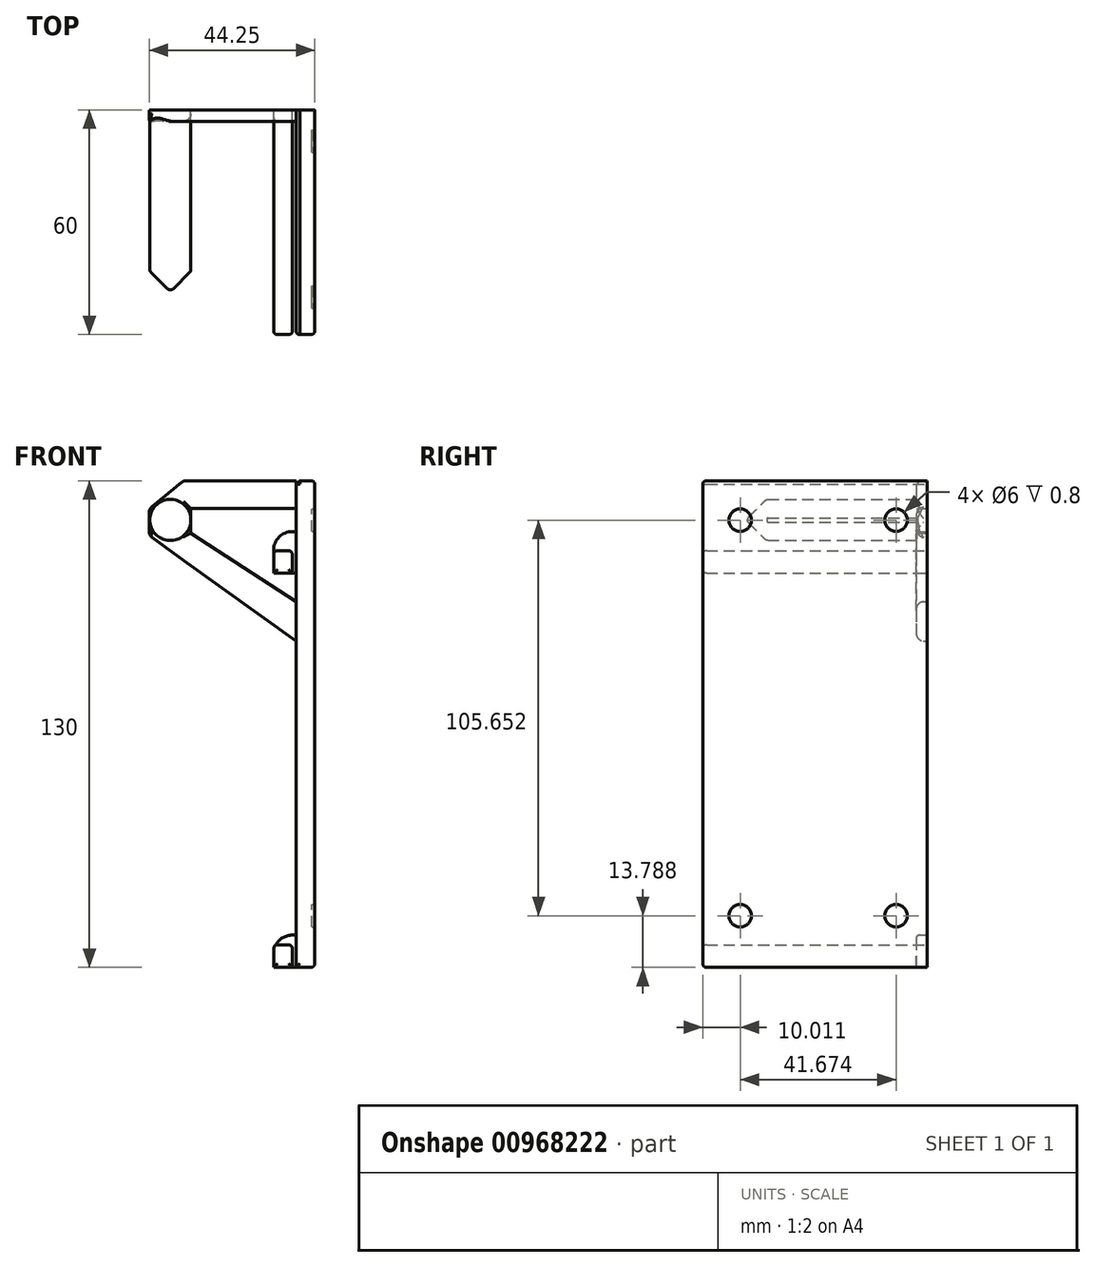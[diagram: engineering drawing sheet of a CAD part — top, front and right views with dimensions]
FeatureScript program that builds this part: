
annotation { "Feature Type Name" : "Feature", "Feature Type Description" : "" }
export const myFeature = defineFeature(function(context is Context, id is Id, definition is map)
    precondition{}
    {
        {
            var Q0;
            Q0=qCreatedBy(makeId("Front.planeOp"),FACE);
            var sketch = newSketch(context, id + "F0", { "sketchPlane" : qUnion([Q0])});
            skLineSegment(sketch, "E0.bottom", {"start": v(0, 55.56) * mm, "end": v(-5, 55.56) * mm});
            skLineSegment(sketch, "E0.top", {"start": v(0, -74.44) * mm, "end": v(-5, -74.44) * mm});
            skLineSegment(sketch, "E0.left", {"start": v(0, 55.56) * mm, "end": v(0, -74.44) * mm});
            skLineSegment(sketch, "E0.right", {"start": v(-5, 55.56) * mm, "end": v(-5, -74.44) * mm});
            skLineSegment(sketch, "E1", {"start": v(-5, 55.56) * mm, "end": v(-35, 55.56) * mm});
            skLineSegment(sketch, "E2", {"start": v(-35, 55.56) * mm, "end": v(-44.25, 47.98) * mm});
            skLineSegment(sketch, "E3", {"start": v(-44.25, 47.98) * mm, "end": v(-44.25, 40.95) * mm});
            skLineSegment(sketch, "E4", {"start": v(-44.25, 40.95) * mm, "end": v(-35, 34.13) * mm});
            skLineSegment(sketch, "E5", {"start": v(-35, 34.13) * mm, "end": v(-5, 12.72) * mm});
            skLineSegment(sketch, "E6", {"start": v(-5, 12.72) * mm, "end": v(-5, 23.2) * mm});
            skLineSegment(sketch, "E7", {"start": v(-5, 23.2) * mm, "end": v(-33.14, 41.58) * mm});
            skLineSegment(sketch, "E8", {"start": v(-33.14, 41.58) * mm, "end": v(-33.14, 48.1) * mm});
            skLineSegment(sketch, "E9", {"start": v(-33.14, 48.1) * mm, "end": v(-5, 48.1) * mm});
            skLineSegment(sketch, "E10", {"start": v(-5, 48.1) * mm, "end": v(-5, 55.56) * mm});
            skLineSegment(sketch, "E11", {"start": v(-5, 23.2) * mm, "end": v(-5, 12.72) * mm});
            skLineSegment(sketch, "E12", {"start": v(-5, -74.44) * mm, "end": v(-6, -74.44) * mm});
            skLineSegment(sketch, "E13", {"start": v(-6, -74.44) * mm, "end": v(-11, -74.44) * mm});
            skLineSegment(sketch, "E14", {"start": v(-11, -74.44) * mm, "end": v(-11, -68.44) * mm});
            skLineSegment(sketch, "E15", {"start": v(-11, -68.44) * mm, "end": v(-6, -68.44) * mm});
            skLineSegment(sketch, "E16", {"start": v(-6, -68.44) * mm, "end": v(-6, -74.44) * mm});
            skLineSegment(sketch, "E17.bottom", {"start": v(-5, -74.44) * mm, "end": v(-11, -74.44) * mm});
            skLineSegment(sketch, "E17.top", {"start": v(-5, -65.81) * mm, "end": v(-11, -65.81) * mm});
            skLineSegment(sketch, "E17.left", {"start": v(-5, -74.44) * mm, "end": v(-5, -65.81) * mm});
            skLineSegment(sketch, "E17.right", {"start": v(-11, -74.44) * mm, "end": v(-11, -65.81) * mm});
            skLineSegment(sketch, "E18", {"start": v(-5, 30.82) * mm, "end": v(-6, 30.82) * mm});
            skLineSegment(sketch, "E19", {"start": v(-6, 30.82) * mm, "end": v(-11, 30.82) * mm});
            skLineSegment(sketch, "E20", {"start": v(-11, 30.82) * mm, "end": v(-11, 36.82) * mm});
            skLineSegment(sketch, "E21", {"start": v(-11, 36.82) * mm, "end": v(-6, 36.82) * mm});
            skLineSegment(sketch, "E22", {"start": v(-6, 36.82) * mm, "end": v(-6, 30.82) * mm});
            skLineSegment(sketch, "E23.bottom", {"start": v(-5, 30.82) * mm, "end": v(-11, 30.82) * mm});
            skLineSegment(sketch, "E23.top", {"start": v(-5, 41.97) * mm, "end": v(-11, 41.97) * mm});
            skLineSegment(sketch, "E23.left", {"start": v(-5, 30.82) * mm, "end": v(-5, 41.97) * mm});
            skLineSegment(sketch, "E23.right", {"start": v(-11, 30.82) * mm, "end": v(-11, 41.97) * mm});
            skSolve(sketch);
        }
        {
            var Q0;
            {var subQ4=sQuery(id+"F0.wireOp",EDGE,"E21");Q0=makeQuery(id+"F0.imprint","IMPRINT",FACE,{"disambiguationData":[TD([[makeQuery(id+"F0.imprint","IMPRINT",EDGE,{"derivedFrom":subQ4}),1.0]])]});}
            var Q1;
            Q1=makeQuery(id+"F0.imprint","IMPRINT",FACE,{"disambiguationData":[TD([[makeQuery(id+"F0.imprint","IMPRINT",EDGE,{"derivedFrom":sQuery(id+"F0.wireOp",EDGE,"E1")}),1.0]])]});
            var Q2;
            {var subQ4=sQuery(id+"F0.wireOp",EDGE,"E15");Q2=makeQuery(id+"F0.imprint","IMPRINT",FACE,{"disambiguationData":[TD([[makeQuery(id+"F0.imprint","IMPRINT",EDGE,{"derivedFrom":subQ4}),1.0]])]});}
            var Q3;
            {var subQ0=sQuery(id+"F0.wireOp",EDGE,"E15");Q3=makeQuery(id+"F0.imprint","IMPRINT",FACE,{"disambiguationData":[TD([[makeQuery(id+"F0.imprint","IMPRINT",EDGE,{"derivedFrom":subQ0}),-1.0]])]});}
            var Q4;
            {var subQ0=sQuery(id+"F0.wireOp",EDGE,"E21");Q4=makeQuery(id+"F0.imprint","IMPRINT",FACE,{"disambiguationData":[TD([[makeQuery(id+"F0.imprint","IMPRINT",EDGE,{"derivedFrom":subQ0}),-1.0]])]});}
            extrude(context, id + "F1", {"entities" : qUnion([Q0, Q1, Q2, Q3, Q4]), "depth" : 3 * mm, "offsetDistance" : 25 * mm});
        }
        {
            var Q0;
            Q0=makeQuery(id+"F0.imprint","IMPRINT",FACE,{"disambiguationData":[TD([[makeQuery(id+"F0.imprint","IMPRINT",EDGE,{"derivedFrom":sQuery(id+"F0.wireOp",EDGE,"E0.bottom")}),1.0]])]});
            var Q1;
            {var subQ0=sQuery(id+"F0.wireOp",EDGE,"E15");Q1=makeQuery(id+"F0.imprint","IMPRINT",FACE,{"disambiguationData":[TD([[makeQuery(id+"F0.imprint","IMPRINT",EDGE,{"derivedFrom":subQ0}),-1.0]])]});}
            var Q2;
            {var subQ0=sQuery(id+"F0.wireOp",EDGE,"E21");Q2=makeQuery(id+"F0.imprint","IMPRINT",FACE,{"disambiguationData":[TD([[makeQuery(id+"F0.imprint","IMPRINT",EDGE,{"derivedFrom":subQ0}),-1.0]])]});}
            extrude(context, id + "F2", {"entities" : qUnion([Q0, Q1, Q2]), "depth" : 60 * mm, "offsetDistance" : 25 * mm});
        }
        {
            var Q0;
            Q0=makeQuery(id+"F1.opExtrude","CAP_FACE",FACE,{"disambiguationData":[OSD([sQuery(id+"F0.wireOp",EDGE,"E1"),sQuery(id+"F0.wireOp",EDGE,"E2"),sQuery(id+"F0.wireOp",EDGE,"E3"),sQuery(id+"F0.wireOp",EDGE,"E4"),sQuery(id+"F0.wireOp",EDGE,"E5"),sQuery(id+"F0.wireOp",EDGE,"E7"),sQuery(id+"F0.wireOp",EDGE,"E8"),sQuery(id+"F0.wireOp",EDGE,"E9"),sQuery(id+"F0.wireOp",EDGE,"E10"),sQuery(id+"F0.wireOp",EDGE,"E11")])],"isStart":false});
            var sketch = newSketch(context, id + "F3", { "sketchPlane" : qUnion([Q0])});
            skCircle(sketch, "E24", {"center": v(-38.6, 45.06) * mm, "radius": 5.5 * mm});
            skSolve(sketch);
        }
        {
            var Q0;
            {var subQ0=sQuery(id+"F3.wireOp",EDGE,"E24");var subQ1=makeQuery(id+"F1.opExtrude","CAP_EDGE",EDGE,{"disambiguationData":[OSD([sQuery(id+"F0.wireOp",EDGE,"E8")])],"isStart":false});var subQ2=makeQuery(id+"F3.imprint","INTERSECT",VERTEX,{"disambiguationData":[OD(0.0)],"derivedFrom":[subQ1,subQ0]});Q0=makeQuery(id+"F3.imprint","IMPRINT",FACE,{"disambiguationData":[TD([[makeQuery(id+"F3.imprint","IMPRINT",EDGE,{"disambiguationData":[TD([[subQ2,1.0]])],"derivedFrom":subQ0}),1.0]])]});}
            extrude(context, id + "F4", {"entities" : qUnion([Q0]), "operationType" : NewBodyOperationType.ADD, "depth" : 45 * mm, "offsetDistance" : 25 * mm});
        }
        {
            var Q0;
            Q0=makeQuery(id+"F4.opExtrude","CAP_EDGE",EDGE,{"disambiguationData":[OSD([sQuery(id+"F3.wireOp",EDGE,"E24")])],"isStart":false});
            chamfer(context, id + "F5", {"entities" : qUnion([Q0]), "width" : 5 * mm, "tangentPropagation" : true});
        }
        {
            var Q0;
            Q0=makeQuery(id+"F1.opExtrude","SWEPT_EDGE",EDGE,{"disambiguationData":[OSD([sQuery(id+"F0.wireOp",EDGE,"E2"),sQuery(id+"F0.wireOp",EDGE,"E3")])]});
            var Q1;
            Q1=makeQuery(id+"F1.opExtrude","SWEPT_EDGE",EDGE,{"disambiguationData":[OSD([sQuery(id+"F0.wireOp",EDGE,"E3"),sQuery(id+"F0.wireOp",EDGE,"E4")])]});
            var Q2;
            Q2=makeQuery(id+"F1.opExtrude","SWEPT_EDGE",EDGE,{"disambiguationData":[OSD([sQuery(id+"F0.wireOp",EDGE,"E1"),sQuery(id+"F0.wireOp",EDGE,"E2")])]});
            var Q3;
            Q3=makeQuery(id+"F1.opExtrude","SWEPT_EDGE",EDGE,{"disambiguationData":[OSD([sQuery(id+"F0.wireOp",EDGE,"E4"),sQuery(id+"F0.wireOp",EDGE,"E5")])]});
            var Q4;
            Q4=makeQuery(id+"F1.opExtrude","CAP_EDGE",EDGE,{"disambiguationData":[OSD([sQuery(id+"F0.wireOp",EDGE,"E5")])],"isStart":false});
            var Q5;
            Q5=makeQuery(id+"F1.opExtrude","CAP_EDGE",EDGE,{"disambiguationData":[OSD([sQuery(id+"F0.wireOp",EDGE,"E7")])],"isStart":false});
            var Q6;
            Q6=makeQuery(id+"F1.opExtrude","CAP_EDGE",EDGE,{"disambiguationData":[OSD([sQuery(id+"F0.wireOp",EDGE,"E4")])],"isStart":false});
            var Q7;
            Q7=makeQuery(id+"F1.opExtrude","CAP_EDGE",EDGE,{"disambiguationData":[OSD([sQuery(id+"F0.wireOp",EDGE,"E1")])],"isStart":false});
            var Q8;
            Q8=makeQuery(id+"F1.opExtrude","CAP_EDGE",EDGE,{"disambiguationData":[OSD([sQuery(id+"F0.wireOp",EDGE,"E9")])],"isStart":false});
            var Q9;
            {var subQ0=sQuery(id+"F0.wireOp",EDGE,"E8");var subQ1=sQuery(id+"F0.wireOp",EDGE,"E7");Q9=makeQuery(id+"F4.boolean.opBoolean","SPLIT",EDGE,{"disambiguationData":[TD([makeQuery(id+"F1.opExtrude","SWEPT_FACE",FACE,{"disambiguationData":[OSD([subQ1])]})])],"derivedFrom":makeQuery(id+"F1.opExtrude","CAP_EDGE",EDGE,{"disambiguationData":[OSD([subQ0])],"isStart":false})});}
            var Q10;
            {var subQ0=sQuery(id+"F0.wireOp",EDGE,"E9");var subQ1=sQuery(id+"F0.wireOp",EDGE,"E8");Q10=makeQuery(id+"F4.boolean.opBoolean","SPLIT",EDGE,{"disambiguationData":[TD([makeQuery(id+"F1.opExtrude","SWEPT_FACE",FACE,{"disambiguationData":[OSD([subQ0])]})])],"derivedFrom":makeQuery(id+"F1.opExtrude","CAP_EDGE",EDGE,{"disambiguationData":[OSD([subQ1])],"isStart":false})});}
            var Q11;
            Q11=makeQuery(id+"F1.opExtrude","CAP_EDGE",EDGE,{"disambiguationData":[OSD([sQuery(id+"F0.wireOp",EDGE,"E2")])],"isStart":false});
            fillet(context, id + "F6", {"entities" : qUnion([Q0, Q1, Q2, Q3, Q4, Q5, Q6, Q7, Q8, Q9, Q10, Q11]), "radius" : 2 * mm, "tangentPropagation" : true, "allowEdgeOverflow" : false});
        }
        {
            var Q0;
            Q0=makeQuery(id+"F1.opExtrude","CAP_EDGE",EDGE,{"disambiguationData":[OSD([sQuery(id+"F0.wireOp",EDGE,"E3")])],"isStart":false});
            var Q1;
            {var subQ0=sQuery(id+"F3.wireOp",EDGE,"E24");Q1=makeQuery(id+"F5.opChamfer","BLEND_EDGE",EDGE,{"blendedFrom":[makeQuery(id+"F4.opExtrude","CAP_EDGE",EDGE,{"disambiguationData":[OSD([subQ0])],"isStart":false}),makeQuery(id+"F4.opExtrude","SWEPT_FACE",FACE,{"disambiguationData":[OSD([subQ0])]})],"blendedInto":[makeQuery(id+"F4.opExtrude","SWEPT_FACE",FACE,{"disambiguationData":[OSD([subQ0])]})]});}
            var Q2;
            {var subQ0=sQuery(id+"F3.wireOp",EDGE,"E24");Q2=makeQuery(id+"F5.opChamfer","BLEND_EDGE",EDGE,{"blendedFrom":[makeQuery(id+"F4.opExtrude","CAP_EDGE",EDGE,{"disambiguationData":[OSD([subQ0])],"isStart":false}),makeQuery(id+"F4.opExtrude","CAP_FACE",FACE,{"disambiguationData":[OSD([sQuery(id+"F0.wireOp",EDGE,"E8"),subQ0])],"isStart":false})],"blendedInto":[makeQuery(id+"F4.opExtrude","CAP_FACE",FACE,{"disambiguationData":[OSD([sQuery(id+"F0.wireOp",EDGE,"E8"),subQ0])],"isStart":false})]});}
            var Q3;
            Q3=makeQuery(id+"F2.opExtrude","SWEPT_EDGE",EDGE,{"disambiguationData":[OSD([sQuery(id+"F0.wireOp",EDGE,"E21"),sQuery(id+"F0.wireOp",EDGE,"E22")])]});
            var Q4;
            Q4=makeQuery(id+"F2.opExtrude","SWEPT_EDGE",EDGE,{"disambiguationData":[OSD([sQuery(id+"F0.wireOp",EDGE,"E21"),sQuery(id+"F0.wireOp",EDGE,"E23.right")])]});
            var Q5;
            Q5=makeQuery(id+"F2.opExtrude","SWEPT_EDGE",EDGE,{"disambiguationData":[OSD([sQuery(id+"F0.wireOp",EDGE,"E23.bottom"),sQuery(id+"F0.wireOp",EDGE,"E23.right")])]});
            var Q6;
            Q6=makeQuery(id+"F2.opExtrude","SWEPT_EDGE",EDGE,{"disambiguationData":[OSD([sQuery(id+"F0.wireOp",EDGE,"E22"),sQuery(id+"F0.wireOp",EDGE,"E23.bottom")])]});
            var Q7;
            Q7=makeQuery(id+"F1.opExtrude","CAP_EDGE",EDGE,{"disambiguationData":[OSD([sQuery(id+"F0.wireOp",EDGE,"E23.right")])],"isStart":false});
            var Q8;
            Q8=makeQuery(id+"F1.opExtrude","CAP_EDGE",EDGE,{"disambiguationData":[OSD([sQuery(id+"F0.wireOp",EDGE,"E23.top")])],"isStart":false});
            var Q9;
            Q9=makeQuery(id+"F1.opExtrude","CAP_EDGE",EDGE,{"disambiguationData":[OSD([sQuery(id+"F0.wireOp",EDGE,"E23.bottom")])],"isStart":false});
            var Q10;
            Q10=makeQuery(id+"F2.opExtrude","SWEPT_EDGE",EDGE,{"disambiguationData":[OSD([sQuery(id+"F0.wireOp",EDGE,"E15"),sQuery(id+"F0.wireOp",EDGE,"E17.right")])]});
            var Q11;
            Q11=makeQuery(id+"F2.opExtrude","SWEPT_EDGE",EDGE,{"disambiguationData":[OSD([sQuery(id+"F0.wireOp",EDGE,"E17.bottom"),sQuery(id+"F0.wireOp",EDGE,"E17.right")])]});
            var Q12;
            Q12=makeQuery(id+"F2.opExtrude","SWEPT_EDGE",EDGE,{"disambiguationData":[OSD([sQuery(id+"F0.wireOp",EDGE,"E15"),sQuery(id+"F0.wireOp",EDGE,"E16")])]});
            var Q13;
            Q13=makeQuery(id+"F2.opExtrude","SWEPT_EDGE",EDGE,{"disambiguationData":[OSD([sQuery(id+"F0.wireOp",EDGE,"E16"),sQuery(id+"F0.wireOp",EDGE,"E17.bottom")])]});
            var Q14;
            Q14=makeQuery(id+"F2.opExtrude","CAP_FACE",FACE,{"disambiguationData":[OSD([sQuery(id+"F0.wireOp",EDGE,"E15"),sQuery(id+"F0.wireOp",EDGE,"E16"),sQuery(id+"F0.wireOp",EDGE,"E17.bottom"),sQuery(id+"F0.wireOp",EDGE,"E17.right")])],"isStart":false});
            var Q15;
            Q15=makeQuery(id+"F2.opExtrude","CAP_FACE",FACE,{"disambiguationData":[OSD([sQuery(id+"F0.wireOp",EDGE,"E21"),sQuery(id+"F0.wireOp",EDGE,"E22"),sQuery(id+"F0.wireOp",EDGE,"E23.bottom"),sQuery(id+"F0.wireOp",EDGE,"E23.right")])],"isStart":false});
            var Q16;
            Q16=makeQuery(id+"F2.opExtrude","CAP_EDGE",EDGE,{"disambiguationData":[OSD([sQuery(id+"F0.wireOp",EDGE,"E0.right"),sQuery(id+"F0.wireOp",EDGE,"E10"),sQuery(id+"F0.wireOp",EDGE,"E11"),sQuery(id+"F0.wireOp",EDGE,"E17.left"),sQuery(id+"F0.wireOp",EDGE,"E23.left")])],"isStart":false});
            var Q17;
            Q17=makeQuery(id+"F2.opExtrude","CAP_EDGE",EDGE,{"disambiguationData":[OSD([sQuery(id+"F0.wireOp",EDGE,"E0.left")])],"isStart":false});
            var Q18;
            Q18=makeQuery(id+"F2.opExtrude","CAP_EDGE",EDGE,{"disambiguationData":[OSD([sQuery(id+"F0.wireOp",EDGE,"E0.top")])],"isStart":false});
            var Q19;
            Q19=makeQuery(id+"F2.opExtrude","CAP_EDGE",EDGE,{"disambiguationData":[OSD([sQuery(id+"F0.wireOp",EDGE,"E0.bottom")])],"isStart":false});
            var Q20;
            Q20=makeQuery(id+"F2.opExtrude","SWEPT_EDGE",EDGE,{"disambiguationData":[OSD([sQuery(id+"F0.wireOp",EDGE,"E0.bottom"),sQuery(id+"F0.wireOp",EDGE,"E0.left")])]});
            var Q21;
            Q21=makeQuery(id+"F2.opExtrude","SWEPT_EDGE",EDGE,{"disambiguationData":[OSD([sQuery(id+"F0.wireOp",EDGE,"E0.top"),sQuery(id+"F0.wireOp",EDGE,"E0.left")])]});
            var Q22;
            Q22=makeQuery(id+"F1.opExtrude","CAP_EDGE",EDGE,{"disambiguationData":[OSD([sQuery(id+"F0.wireOp",EDGE,"E17.right")])],"isStart":false});
            var Q23;
            Q23=makeQuery(id+"F1.opExtrude","CAP_EDGE",EDGE,{"disambiguationData":[OSD([sQuery(id+"F0.wireOp",EDGE,"E17.top")])],"isStart":false});
            var Q24;
            Q24=makeQuery(id+"F1.opExtrude","CAP_EDGE",EDGE,{"disambiguationData":[OSD([sQuery(id+"F0.wireOp",EDGE,"E17.bottom")])],"isStart":false});
            fillet(context, id + "F7", {"entities" : qUnion([Q0, Q1, Q2, Q3, Q4, Q5, Q6, Q7, Q8, Q9, Q10, Q11, Q12, Q13, Q14, Q15, Q16, Q17, Q18, Q19, Q20, Q21, Q22, Q23, Q24]), "radius" : 1 * mm, "tangentPropagation" : true, "allowEdgeOverflow" : false});
        }
        {
            var Q0;
            Q0=makeQuery(id+"F2.opExtrude","SWEPT_FACE",FACE,{"disambiguationData":[OSD([sQuery(id+"F0.wireOp",EDGE,"E0.left")])]});
            var sketch = newSketch(context, id + "F8", { "sketchPlane" : qUnion([Q0])});
            skLineSegment(sketch, "E25.bottom", {"start": v(-8.32, -60.65) * mm, "end": v(-49.99, -60.65) * mm, "construction": true});
            skLineSegment(sketch, "E25.top", {"start": v(-8.32, 45) * mm, "end": v(-49.99, 45) * mm, "construction": true});
            skLineSegment(sketch, "E25.left", {"start": v(-8.32, -60.65) * mm, "end": v(-8.32, 45) * mm, "construction": true});
            skLineSegment(sketch, "E25.right", {"start": v(-49.99, -60.65) * mm, "end": v(-49.99, 45) * mm, "construction": true});
            skCircle(sketch, "E26", {"center": v(-49.99, 45) * mm, "radius": 3 * mm});
            skCircle(sketch, "E27", {"center": v(-8.32, 45) * mm, "radius": 3 * mm});
            skCircle(sketch, "E28", {"center": v(-49.99, -60.65) * mm, "radius": 3 * mm});
            skCircle(sketch, "E29", {"center": v(-8.32, -60.65) * mm, "radius": 3 * mm});
            skSolve(sketch);
        }
        {
            var Q0;
            Q0=makeQuery(id+"F8.imprint","IMPRINT",FACE,{"disambiguationData":[TD([[makeQuery(id+"F8.imprint","IMPRINT",EDGE,{"derivedFrom":sQuery(id+"F8.wireOp",EDGE,"E26")}),1.0]])]});
            var Q1;
            Q1=makeQuery(id+"F8.imprint","IMPRINT",FACE,{"disambiguationData":[TD([[makeQuery(id+"F8.imprint","IMPRINT",EDGE,{"derivedFrom":sQuery(id+"F8.wireOp",EDGE,"E27")}),1.0]])]});
            var Q2;
            Q2=makeQuery(id+"F8.imprint","IMPRINT",FACE,{"disambiguationData":[TD([[makeQuery(id+"F8.imprint","IMPRINT",EDGE,{"derivedFrom":sQuery(id+"F8.wireOp",EDGE,"E28")}),1.0]])]});
            var Q3;
            Q3=makeQuery(id+"F8.imprint","IMPRINT",FACE,{"disambiguationData":[TD([[makeQuery(id+"F8.imprint","IMPRINT",EDGE,{"derivedFrom":sQuery(id+"F8.wireOp",EDGE,"E29")}),1.0]])]});
            extrude(context, id + "F9", {"entities" : qUnion([Q0, Q1, Q2, Q3]), "operationType" : NewBodyOperationType.REMOVE, "oppositeDirection" : true, "depth" : .8 * mm, "offsetDistance" : 25 * mm});
        }
        {
            var Q0;
            Q0=makeQuery(id+"F2.opExtrude","SWEPT_EDGE",EDGE,{"disambiguationData":[OSD([sQuery(id+"F0.wireOp",EDGE,"E0.bottom"),sQuery(id+"F0.wireOp",EDGE,"E1"),sQuery(id+"F0.wireOp",EDGE,"E10")])]});
            chamfer(context, id + "F10", {"entities" : qUnion([Q0]), "width" : 1 * mm, "tangentPropagation" : true});
        }
        {
            var Q0;
            Q0=makeQuery(id+"F1.opExtrude","SWEPT_EDGE",EDGE,{"disambiguationData":[OSD([sQuery(id+"F0.wireOp",EDGE,"E17.top"),sQuery(id+"F0.wireOp",EDGE,"E17.right")])]});
            var Q1;
            Q1=makeQuery(id+"F1.opExtrude","SWEPT_EDGE",EDGE,{"disambiguationData":[OSD([sQuery(id+"F0.wireOp",EDGE,"E23.top"),sQuery(id+"F0.wireOp",EDGE,"E23.right")])]});
            fillet(context, id + "F11", {"entities" : qUnion([Q0, Q1]), "radius" : 5 * mm, "tangentPropagation" : true, "allowEdgeOverflow" : false});
        }
    });
